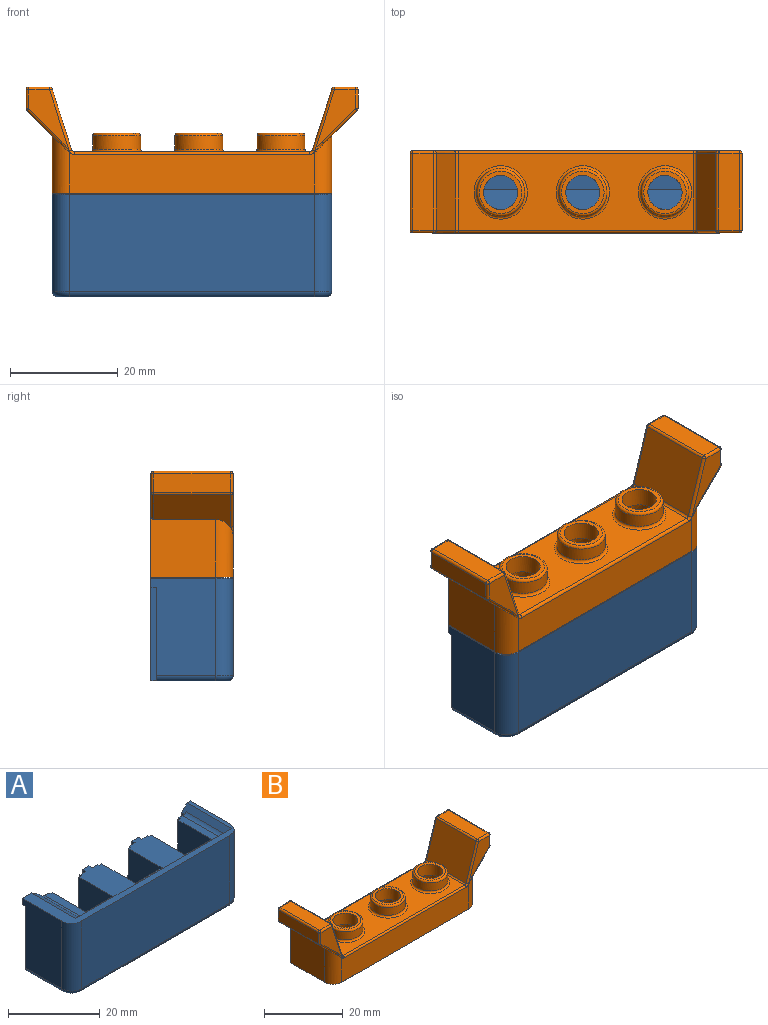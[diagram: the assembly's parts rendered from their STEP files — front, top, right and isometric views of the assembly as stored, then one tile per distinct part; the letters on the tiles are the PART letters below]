
ASSEMBLY  parts=2 mates=1
PART A: 64 faces, bbox 52.4x15.5x19.1 mm
  f0: plane 8.2x0.86mm, normal (0,1,0.01), area 7.1mm2, adj f2,f12,f62,f63
  f1: cylinder r=4.5mm len=9mm, axis (1,0,0), area 110.1mm2, adj f2,f3,f62,f63
  f2: plane 8.17x6.34mm, normal (0,0.81,0.59), area 63.1mm2, adj f0,f1,f62,f63
  f3: plane 7.63x5.76mm, normal (0,0,1), area 43.9mm2, adj f1,f23,f62,f63
  f4: plane 8.2x0.86mm, normal (0,1,0.01), area 7.1mm2, adj f6,f12,f60,f61
  f5: cylinder r=4.5mm len=9mm, axis (1,0,0), area 110.1mm2, adj f6,f7,f60,f61
  f6: plane 8.17x6.34mm, normal (0,0.81,0.59), area 63.1mm2, adj f4,f5,f60,f61
  f7: plane 7.63x5.76mm, normal (0,0,1), area 43.9mm2, adj f5,f25,f60,f61
  f8: plane 8.2x0.86mm, normal (0,1,0.01), area 7.1mm2, adj f10,f12,f58,f59
  f9: cylinder r=4.5mm len=9mm, axis (1,0,0), area 110.1mm2, adj f10,f11,f58,f59
  f10: plane 8.17x6.34mm, normal (0,0.81,0.59), area 63.1mm2, adj f8,f9,f58,f59
  f11: plane 7.63x5.76mm, normal (0,0,1), area 43.9mm2, adj f9,f26,f58,f59
  f12: plane 42.59x13.68mm, normal (0,0,1), area 276mm2, adj f0,f4,f8,f18,f19,f20,f21,f22
  f13: plane 51.87x15.25mm, normal (0,0,1), area 130.4mm2, adj f15,f16,f24,f28,f29,f40,f46,f47
  f14: plane 49.84x14.24mm, normal (0,0,-1), area 652.3mm2, adj f16,f17,f18,f19,f20,f21,f22,f23
  f15: plane 18.03x12.08mm, normal (-1,0,0), area 201.2mm2, adj f13,f17,f40,f48,f51,f53
  f16: plane 19.05x2.82mm, normal (0,1,0), area 52mm2, adj f13,f14,f28,f39,f46,f57
  f17: plane 17.4x3.49mm, normal (0,1,0), area 60.5mm2, adj f14,f15,f42,f48,f53
  f18: plane 17.81x2.21mm, normal (0,1,0), area 30.6mm2, adj f12,f14,f35,f39,f46,f50
  f19: plane 17.4x1.75mm, normal (0,1,0), area 30.5mm2, adj f12,f14,f32,f38
  f20: plane 17.4x1.75mm, normal (0,1,0), area 30.5mm2, adj f12,f14,f34,f37
  f21: plane 17.4x1.75mm, normal (0,1,0), area 30.5mm2, adj f12,f14,f31,f45
  f22: plane 17.67x2.16mm, normal (0,1,0), area 30.5mm2, adj f12,f14,f33,f41,f47,f49
  f23: plane 17.4x9.7mm, normal (0,1,0), area 40.5mm2, adj f3,f12,f14,f31,f33,f62,f63
  f24: plane 48x1.65mm, normal (0,1,0), area 75.6mm2, adj f12,f13,f46,f47,f49,f50
  f25: plane 17.4x9.7mm, normal (0,1,0), area 40.5mm2, adj f7,f12,f14,f30,f32,f60,f61
  f26: plane 17.4x9.7mm, normal (0,1,0), area 40.5mm2, adj f11,f12,f14,f34,f35,f58,f59
  f27: plane 17.4x1.75mm, normal (0,1,0), area 30.5mm2, adj f12,f14,f30,f44
  f28: plane 18.03x12.08mm, normal (1,0,0), area 217.8mm2, adj f13,f16,f52,f57
  f29: plane 45.52x18.03mm, normal (0,-1,0), area 820.9mm2, adj f13,f51,f52,f55
  f30: plane 17.4x0.43mm, normal (1,0,0), area 7.5mm2, adj f12,f14,f25,f27
  f31: plane 17.4x0.43mm, normal (-1,0,0), area 7.5mm2, adj f12,f14,f21,f23
  f32: plane 17.4x0.43mm, normal (-1,0,0), area 7.5mm2, adj f12,f14,f19,f25
  f33: plane 17.4x0.43mm, normal (1,0,0), area 7.5mm2, adj f12,f14,f22,f23
  f34: plane 17.4x0.43mm, normal (1,0,0), area 7.5mm2, adj f12,f14,f20,f26
  f35: plane 17.4x0.43mm, normal (-1,0,0), area 7.5mm2, adj f12,f14,f18,f26
  f36: plane 17.4x2.03mm, normal (0,1,0), area 35.4mm2, adj f12,f14,f37,f38
  f37: plane 17.4x1.02mm, normal (1,0,0), area 17.7mm2, adj f12,f14,f20,f36
  f38: plane 17.4x1.02mm, normal (-1,0,0), area 17.7mm2, adj f12,f14,f19,f36
  f39: plane 17.4x1.02mm, normal (-1,0,0), area 17.7mm2, adj f14,f16,f18,f46
  f40: plane 19.05x5.36mm, normal (0,1,0), area 39.3mm2, adj f13,f14,f15,f41,f42,f47,f48
  f41: plane 17.4x1.02mm, normal (1,0,0), area 17.7mm2, adj f14,f22,f40,f47
  f42: plane 17.4x1.02mm, normal (-1,0,0), area 17.7mm2, adj f14,f17,f40,f48
  f43: plane 17.4x2.03mm, normal (0,1,0), area 35.4mm2, adj f12,f14,f44,f45
  f44: plane 17.4x1.02mm, normal (1,0,0), area 17.7mm2, adj f12,f14,f27,f43
  f45: plane 17.4x1.02mm, normal (-1,0,0), area 17.7mm2, adj f12,f14,f21,f43
  f46: plane 13.68x1.82mm, normal (-0.67,0,0.74), area 25.8mm2, adj f13,f16,f18,f24,f39,f50
  f47: plane 13.68x2.49mm, normal (0.55,0,0.83), area 34.8mm2, adj f13,f22,f24,f40,f41,f49
  f48: plane 3.49x1.02mm, normal (0,0,-1), area 3.5mm2, adj f15,f17,f40,f42
  f49: cylinder r=1.6mm len=12.66mm, axis (0,1,0), area 11.9mm2, adj f12,f22,f24,f47
  f50: cylinder r=1.6mm len=12.66mm, axis (0,1,0), area 14.9mm2, adj f12,f18,f24,f46
  f51: cylinder r=3.17mm len=18.03mm, axis (0,0,1), area 89.9mm2, adj f13,f15,f29,f54
  f52: cylinder r=3.17mm len=18.03mm, axis (0,0,1), area 89.9mm2, adj f13,f28,f29,f56
  f53: cylinder r=1.02mm len=11.06mm, axis (0,1,0), area 17.7mm2, adj f14,f15,f17,f54
  f54: torus R=2.16mm, axis (0,0,1), area 7mm2, adj f14,f51,f53,f55
  f55: cylinder r=1.02mm len=45.52mm, axis (-1,0,0), area 72.6mm2, adj f14,f29,f54,f56
  f56: torus R=2.16mm, axis (0,0,1), area 7mm2, adj f14,f52,f55,f57
  f57: cylinder r=1.02mm len=12.08mm, axis (0,-1,0), area 19.3mm2, adj f14,f16,f28,f56
  f58: plane 16.2x10.36mm, normal (-1,0,0.02), area 143.6mm2, adj f8,f9,f10,f11,f12,f26
  f59: plane 16.2x10.36mm, normal (1,0,0.02), area 143.6mm2, adj f8,f9,f10,f11,f12,f26
  f60: plane 16.2x10.36mm, normal (-1,0,0.02), area 143.6mm2, adj f4,f5,f6,f7,f12,f25
  f61: plane 16.2x10.36mm, normal (1,0,0.02), area 143.6mm2, adj f4,f5,f6,f7,f12,f25
  f62: plane 16.2x10.36mm, normal (-1,0,0.02), area 143.6mm2, adj f0,f1,f2,f3,f12,f23
  f63: plane 16.2x10.36mm, normal (1,0,0.02), area 143.6mm2, adj f0,f1,f2,f3,f12,f23
PART B: 178 faces, bbox 62.3x15.9x22.2 mm
  f0: plane 12.29x11.58mm, normal (1,0,0), area 123.2mm2, adj f2,f39,f57,f62,f100,f108,f109,f110
  f1: plane 43.74x14.25mm, normal (0,0,1), area 392.2mm2, adj f33,f34,f35,f81,f82,f91,f92
  f2: plane 60.6x20.93mm, normal (0,1,0), area 287.2mm2, adj f0,f8,f9,f10,f11,f14,f16,f17
  f3: plane 60.6x19.17mm, normal (0,-1,0), area 394.2mm2, adj f39,f62,f63,f67,f72,f80,f86,f87
  f4: plane 42.71x12.9mm, normal (0,0,-1), area 300mm2, adj f12,f13,f15,f18,f21,f22,f40,f41
  f5: cylinder r=3.17mm len=6.35mm, axis (0,0,-1), area 68.9mm2, adj f28,f53
  f6: cylinder r=3.17mm len=6.35mm, axis (0,0,-1), area 68.9mm2, adj f26,f52
  f7: cylinder r=3.17mm len=6.35mm, axis (0,0,-1), area 68.9mm2, adj f24,f51
  f8: plane 4.57x1.02mm, normal (1,0,0), area 4.6mm2, adj f2,f16,f22,f50
  f9: plane 4.57x1.02mm, normal (-1,0,0), area 4.6mm2, adj f2,f14,f22,f50
  f10: plane 4.57x1.02mm, normal (-1,0,0), area 4.6mm2, adj f2,f17,f22,f49
  f11: plane 4.57x1.02mm, normal (1,0,0), area 4.6mm2, adj f2,f14,f22,f49
  f12: plane 9.7x2.54mm, normal (0,1,0), area 24.6mm2, adj f4,f30,f43,f45
  f13: plane 9.7x2.54mm, normal (0,1,0), area 24.6mm2, adj f4,f32,f41,f42
  f14: plane 13.21x1.02mm, normal (0,0,-1), area 13.4mm2, adj f2,f9,f11,f22
  f15: plane 9.7x2.54mm, normal (0,1,0), area 24.6mm2, adj f4,f31,f40,f44
  f16: plane 13.21x1.02mm, normal (0,0,-1), area 13.4mm2, adj f2,f8,f22,f48
  f17: plane 13.21x1.02mm, normal (0,0,-1), area 13.4mm2, adj f2,f10,f22,f46
  f18: cylinder r=1.7mm len=13.42mm, axis (0,1,0), area 15.7mm2, adj f2,f4,f19,f21,f22,f48
  f19: plane 13.42x1.59mm, normal (0.67,0,-0.75), area 28.6mm2, adj f2,f18,f21,f39
  f20: plane 13.42x2.04mm, normal (-0.6,0,-0.8), area 34.1mm2, adj f2,f21,f39,f47
  f21: plane 48x1.85mm, normal (0,-1,0), area 84.5mm2, adj f4,f18,f19,f20,f39,f47
  f22: plane 43.69x6.22mm, normal (0,1,0), area 179.3mm2, adj f4,f8,f9,f10,f11,f14,f16,f17
  f23: plane 12.29x11.58mm, normal (-1,0,0), area 129mm2, adj f2,f39,f58,f63,f98
  f24: plane 7.87x7.87mm, normal (0,0,1), area 17mm2, adj f7,f36
  f25: cylinder r=4.45mm len=8.89mm, axis (0,0,-1), area 68.1mm2, adj f35,f36
  f26: plane 7.87x7.87mm, normal (0,0,1), area 17mm2, adj f6,f37
  f27: cylinder r=4.45mm len=8.89mm, axis (0,0,-1), area 68.1mm2, adj f34,f37
  f28: plane 7.87x7.87mm, normal (0,0,1), area 17mm2, adj f5,f38
  f29: cylinder r=4.45mm len=8.89mm, axis (0,0,-1), area 68.1mm2, adj f33,f38
  f30: plane 9.7x0.43mm, normal (0,0,-1), area 4.2mm2, adj f12,f22,f43,f45
  f31: plane 9.7x0.43mm, normal (0,0,-1), area 4.2mm2, adj f15,f22,f40,f44
  f32: plane 9.7x0.43mm, normal (0,0,-1), area 4.2mm2, adj f13,f22,f41,f42
  f33: torus R=4.95mm, axis (0,0,-1), area 23.2mm2, adj f1,f29
  f34: torus R=4.95mm, axis (0,0,-1), area 23.2mm2, adj f1,f27
  f35: torus R=4.95mm, axis (0,0,-1), area 23.2mm2, adj f1,f25
  f36: torus R=3.94mm, axis (0,0,1), area 21.4mm2, adj f24,f25
  f37: torus R=3.94mm, axis (0,0,1), area 21.4mm2, adj f26,f27
  f38: torus R=3.94mm, axis (0,0,1), area 21.4mm2, adj f28,f29
  f39: plane 51.87x15.25mm, normal (0,0,-1), area 142.6mm2, adj f0,f2,f3,f19,f20,f21,f23,f62
  f40: plane 2.54x0.43mm, normal (-1,0,0), area 1.1mm2, adj f4,f15,f22,f31
  f41: plane 2.54x0.43mm, normal (1,0,0), area 1.1mm2, adj f4,f13,f22,f32
  f42: plane 2.54x0.43mm, normal (-1,0,0), area 1.1mm2, adj f4,f13,f22,f32
  f43: plane 2.54x0.43mm, normal (1,0,0), area 1.1mm2, adj f4,f12,f22,f30
  f44: plane 2.54x0.43mm, normal (1,0,0), area 1.1mm2, adj f4,f15,f22,f31
  f45: plane 2.54x0.43mm, normal (-1,0,0), area 1.1mm2, adj f4,f12,f22,f30
  f46: plane 6.13x1.02mm, normal (1,0,0), area 6.2mm2, adj f2,f17,f22,f47
  f47: cylinder r=1.7mm len=13.42mm, axis (0,1,0), area 14mm2, adj f2,f4,f20,f21,f22,f46
  f48: plane 5.96x1.02mm, normal (-1,0,0), area 6.1mm2, adj f2,f16,f18,f22
  f49: plane 2.03x1.02mm, normal (0,0,-1), area 2.1mm2, adj f2,f10,f11,f22
  f50: plane 2.03x1.02mm, normal (0,0,-1), area 2.1mm2, adj f2,f8,f9,f22
  f51: bspline ~9.53x8.64mm, area 249.1mm2, adj f4,f7
  f52: bspline ~9.53x8.64mm, area 249.1mm2, adj f4,f6
  f53: bspline ~9.53x8.64mm, area 249.1mm2, adj f4,f5
  f54: plane 14.25x11.3mm, normal (-0.95,0,0.3), area 169.1mm2, adj f83,f92,f93,f97
  f55: plane 14.25x3.88mm, normal (0,0,1), area 55.3mm2, adj f84,f85,f93,f94
  f56: plane 14.25x3.51mm, normal (1,0,0), area 50mm2, adj f75,f79,f85,f86
  f57: plane 14.93x6.85mm, normal (0.7,0,-0.71), area 95.8mm2, adj f0,f62,f79,f100,f106
  f58: plane 14.93x6.85mm, normal (-0.7,0,-0.71), area 95.8mm2, adj f23,f63,f65,f98,f103
  f59: plane 14.25x3.51mm, normal (-1,0,0), area 50mm2, adj f64,f65,f67,f68
  f60: plane 14.25x3.88mm, normal (0,0,1), area 55.3mm2, adj f68,f69,f72,f73
  f61: plane 14.25x11.3mm, normal (0.95,0,0.3), area 169.1mm2, adj f73,f74,f80,f81
  f62: cylinder r=3.17mm len=10.67mm, axis (0,0,-1), area 46.8mm2, adj f0,f3,f39,f57,f105
  f63: cylinder r=3.17mm len=10.67mm, axis (0,0,1), area 46.8mm2, adj f3,f23,f39,f58,f102
  f64: cylinder r=0.5mm len=3.51mm, axis (0,0,1), area 2.8mm2, adj f2,f59,f66,f99
  f65: cylinder r=0.5mm len=14.25mm, axis (0,1,0), area 5.7mm2, adj f58,f59,f99,f104
  f66: sphere r=0.5mm, area 0.4mm2, adj f64,f68,f69
  f67: cylinder r=0.5mm len=3.51mm, axis (0,0,1), area 2.8mm2, adj f3,f59,f70,f104
  f68: cylinder r=0.5mm len=14.25mm, axis (0,1,0), area 11.2mm2, adj f59,f60,f66,f70
  f69: cylinder r=0.5mm len=3.88mm, axis (1,0,0), area 3mm2, adj f2,f60,f66,f71
  f70: sphere r=0.5mm, area 0.4mm2, adj f67,f68,f72
  f71: sphere r=0.5mm, area 0.3mm2, adj f69,f73,f74
  f72: cylinder r=0.5mm len=3.88mm, axis (1,0,0), area 3mm2, adj f3,f60,f70,f76
  f73: cylinder r=0.5mm len=14.25mm, axis (0,1,0), area 9mm2, adj f60,f61,f71,f76
  f74: cylinder r=0.5mm len=11.45mm, axis (0.3,0,-0.95), area 9.3mm2, adj f2,f61,f71,f77
  f75: cylinder r=0.5mm len=3.51mm, axis (0,0,-1), area 2.8mm2, adj f2,f56,f78,f101
  f76: sphere r=0.5mm, area 0.3mm2, adj f72,f73,f80
  f77: torus R=1mm, axis (0,1,0), area 0.7mm2, adj f2,f74,f81,f82
  f78: sphere r=0.5mm, area 0.4mm2, adj f75,f84,f85
  f79: cylinder r=0.5mm len=14.25mm, axis (0,1,0), area 5.7mm2, adj f56,f57,f101,f107
  f80: cylinder r=0.5mm len=11.45mm, axis (0.3,0,-0.95), area 9.3mm2, adj f3,f61,f76,f87
  f81: cylinder r=0.5mm len=14.25mm, axis (0,-1,0), area 9mm2, adj f1,f61,f77,f87
  f82: cylinder r=0.5mm len=43.74mm, axis (1,0,0), area 34.4mm2, adj f1,f2,f77,f88
  f83: cylinder r=0.5mm len=11.45mm, axis (0.3,0,0.95), area 9.3mm2, adj f2,f54,f88,f89
  f84: cylinder r=0.5mm len=3.88mm, axis (1,0,0), area 3mm2, adj f2,f55,f78,f89
  f85: cylinder r=0.5mm len=14.25mm, axis (0,1,0), area 11.2mm2, adj f55,f56,f78,f90
  f86: cylinder r=0.5mm len=3.51mm, axis (0,0,-1), area 2.8mm2, adj f3,f56,f90,f107
  f87: torus R=1mm, axis (0,-1,0), area 0.7mm2, adj f3,f80,f81,f91
  f88: torus R=1mm, axis (0,1,0), area 0.7mm2, adj f2,f82,f83,f92
  f89: sphere r=0.5mm, area 0.5mm2, adj f83,f84,f93
  f90: sphere r=0.5mm, area 0.4mm2, adj f85,f86,f94
  f91: cylinder r=0.5mm len=43.74mm, axis (-1,0,0), area 34.4mm2, adj f1,f3,f87,f95
  f92: cylinder r=0.5mm len=14.25mm, axis (0,1,0), area 9mm2, adj f1,f54,f88,f95
  f93: cylinder r=0.5mm len=14.25mm, axis (0,1,0), area 9mm2, adj f54,f55,f89,f96
  f94: cylinder r=0.5mm len=3.88mm, axis (1,0,0), area 3mm2, adj f3,f55,f90,f96
  f95: torus R=1mm, axis (0,-1,0), area 0.7mm2, adj f3,f91,f92,f97
  f96: sphere r=0.5mm, area 0.3mm2, adj f93,f94,f97
  f97: cylinder r=0.5mm len=11.45mm, axis (0.3,0,0.95), area 9.3mm2, adj f3,f54,f95,f96
  f98: cylinder r=0.5mm len=5.06mm, axis (-0.71,0,0.7), area 5mm2, adj f2,f23,f58,f99
  f99: sphere r=0.5mm, area 0.1mm2, adj f64,f65,f98
  f100: cylinder r=0.5mm len=5.06mm, axis (-0.71,0,-0.7), area 5mm2, adj f0,f2,f57,f101
  f101: sphere r=0.5mm, area 0.1mm2, adj f75,f79,f100
  f102: bspline ~2.04x1.71mm, area 0.6mm2, adj f3,f63,f103
  f103: cylinder r=0.5mm len=6.53mm, axis (-0.71,0,0.7), area 6.8mm2, adj f3,f58,f102,f104
  f104: sphere r=0.5mm, area 0.1mm2, adj f65,f67,f103
  f105: bspline ~2.24x1.97mm, area 0.6mm2, adj f3,f62,f106
  f106: cylinder r=0.5mm len=6.53mm, axis (-0.71,0,-0.7), area 6.8mm2, adj f3,f57,f105,f107
  f107: sphere r=0.5mm, area 0.2mm2, adj f79,f86,f106
  f108: extruded ~1x0.31mm, area 0.3mm2, adj f0,f109,f135,f136
  f109: extruded ~1x0.36mm, area 0.4mm2, adj f0,f108,f110,f136
  f110: extruded ~1x0.45mm, area 0.5mm2, adj f0,f109,f111,f136
  f111: extruded ~1x0.34mm, area 0.3mm2, adj f0,f110,f112,f136
  f112: extruded ~1x0.28mm, area 0.3mm2, adj f0,f111,f113,f136
  f113: plane 1x0.15mm, normal (0,0.8,0.6), area 0.2mm2, adj f0,f112,f114,f136
  f114: extruded ~1x0.26mm, area 0.3mm2, adj f0,f113,f115,f136
  f115: extruded ~1x0.25mm, area 0.2mm2, adj f0,f114,f116,f136
  f116: extruded ~1x0.27mm, area 0.3mm2, adj f0,f115,f117,f136
  f117: extruded ~1x0.23mm, area 0.3mm2, adj f0,f116,f118,f136
  f118: extruded ~1x0.28mm, area 0.3mm2, adj f0,f117,f119,f136
  f119: extruded ~1x0.37mm, area 0.4mm2, adj f0,f118,f120,f136
  f120: plane 1x0.2mm, normal (0,0,-1), area 0.2mm2, adj f0,f119,f121,f136
  f121: plane 1x0.19mm, normal (0,1,0), area 0.2mm2, adj f0,f120,f122,f136
  f122: plane 1x0.2mm, normal (0,0,1), area 0.2mm2, adj f0,f121,f123,f136
  f123: extruded ~1x0.57mm, area 0.8mm2, adj f0,f122,f124,f136
  f124: extruded ~1x0.51mm, area 0.7mm2, adj f0,f123,f125,f136
  f125: extruded ~1x0.28mm, area 0.3mm2, adj f0,f124,f126,f136
  f126: extruded ~1x0.27mm, area 0.3mm2, adj f0,f125,f127,f136
  f127: plane 1x0.21mm, normal (0,1,0), area 0.2mm2, adj f0,f126,f128,f136
  f128: extruded ~1x0.25mm, area 0.3mm2, adj f0,f127,f129,f136
  f129: extruded ~1x0.29mm, area 0.3mm2, adj f0,f128,f130,f136
  f130: extruded ~1x0.56mm, area 0.6mm2, adj f0,f129,f131,f136
  f131: extruded ~1x0.44mm, area 0.5mm2, adj f0,f130,f132,f136
  f132: extruded ~1x0.32mm, area 0.3mm2, adj f0,f131,f133,f136
  f133: extruded ~1x0.35mm, area 0.4mm2, adj f0,f132,f134,f136
  f134: plane 1x0.01mm, normal (0,-1,0), area 0mm2, adj f0,f133,f135,f136
  f135: extruded ~1x0.3mm, area 0.3mm2, adj f0,f108,f134,f136
  f136: plane 2.04x1.3mm, normal (1,0,0), area 0.9mm2, adj f108,f109,f110,f111,f112,f113,f114,f115
  f137: extruded ~1x0.63mm, area 0.6mm2, adj f138,f152,f153,f176
  f138: extruded ~1x0.63mm, area 0.6mm2, adj f137,f139,f153,f176
  f139: extruded ~1x0.32mm, area 0.4mm2, adj f138,f140,f153,f176
  f140: extruded ~1x0.33mm, area 0.4mm2, adj f139,f141,f153,f176
  f141: extruded ~1x0.63mm, area 0.6mm2, adj f140,f142,f153,f176
  f142: extruded ~1x0.63mm, area 0.6mm2, adj f141,f143,f153,f176
  f143: extruded ~1x0.33mm, area 0.4mm2, adj f142,f152,f153,f176
  f144: extruded ~1x0.77mm, area 0.8mm2, adj f0,f145,f151,f153
  f145: extruded ~1x0.76mm, area 0.8mm2, adj f0,f144,f146,f153
  f146: extruded ~1x0.49mm, area 0.6mm2, adj f0,f145,f147,f153
  f147: extruded ~1x0.49mm, area 0.6mm2, adj f0,f146,f148,f153
  f148: extruded ~1x0.77mm, area 0.8mm2, adj f0,f147,f149,f153
  f149: extruded ~1x0.76mm, area 0.8mm2, adj f0,f148,f150,f153
  f150: extruded ~1x0.49mm, area 0.6mm2, adj f0,f149,f151,f153
  f151: extruded ~1x0.5mm, area 0.6mm2, adj f0,f144,f150,f153
  f152: extruded ~1x0.32mm, area 0.4mm2, adj f137,f143,f153,f176
  f153: plane 2.04x1.31mm, normal (1,0,0), area 1mm2, adj f137,f138,f139,f140,f141,f142,f143,f144
  f154: extruded ~1x0.63mm, area 0.6mm2, adj f155,f169,f170,f177
  f155: extruded ~1x0.63mm, area 0.6mm2, adj f154,f156,f170,f177
  f156: extruded ~1x0.32mm, area 0.4mm2, adj f155,f157,f170,f177
  f157: extruded ~1x0.33mm, area 0.4mm2, adj f156,f158,f170,f177
  f158: extruded ~1x0.63mm, area 0.6mm2, adj f157,f159,f170,f177
  f159: extruded ~1x0.63mm, area 0.6mm2, adj f158,f160,f170,f177
  f160: extruded ~1x0.33mm, area 0.4mm2, adj f159,f169,f170,f177
  f161: extruded ~1x0.77mm, area 0.8mm2, adj f0,f162,f168,f170
  f162: extruded ~1x0.76mm, area 0.8mm2, adj f0,f161,f163,f170
  f163: extruded ~1x0.49mm, area 0.6mm2, adj f0,f162,f164,f170
  f164: extruded ~1x0.49mm, area 0.6mm2, adj f0,f163,f165,f170
  f165: extruded ~1x0.77mm, area 0.8mm2, adj f0,f164,f166,f170
  f166: extruded ~1x0.76mm, area 0.8mm2, adj f0,f165,f167,f170
  f167: extruded ~1x0.49mm, area 0.6mm2, adj f0,f166,f168,f170
  f168: extruded ~1x0.5mm, area 0.6mm2, adj f0,f161,f167,f170
  f169: extruded ~1x0.32mm, area 0.4mm2, adj f154,f160,f170,f177
  f170: plane 2.04x1.31mm, normal (1,0,0), area 1mm2, adj f154,f155,f156,f157,f158,f159,f160,f161
  f171: plane 1.98x1mm, normal (0,1,0), area 2mm2, adj f0,f172,f174,f175
  f172: plane 1x0.23mm, normal (0,0,1), area 0.2mm2, adj f0,f171,f173,f175
  f173: plane 1.98x1mm, normal (0,-1,0), area 2mm2, adj f0,f172,f174,f175
  f174: plane 1x0.23mm, normal (0,0,-1), area 0.2mm2, adj f0,f171,f173,f175
  f175: plane 1.98x0.23mm, normal (1,0,0), area 0.5mm2, adj f171,f172,f173,f174
  f176: plane 1.65x0.85mm, normal (1,0,0), area 1.2mm2, adj f137,f138,f139,f140,f141,f142,f143,f152
  f177: plane 1.65x0.85mm, normal (1,0,0), area 1.2mm2, adj f154,f155,f156,f157,f158,f159,f160,f169
PLACE A t=(-6.54,5.55,9.39)mm
PLACE B t=(-6.54,5.55,9.39)mm
MATE fastened A.f13 <-> B.f50  axis (0,0,1) through (45.43,5.55,11.04)mm
